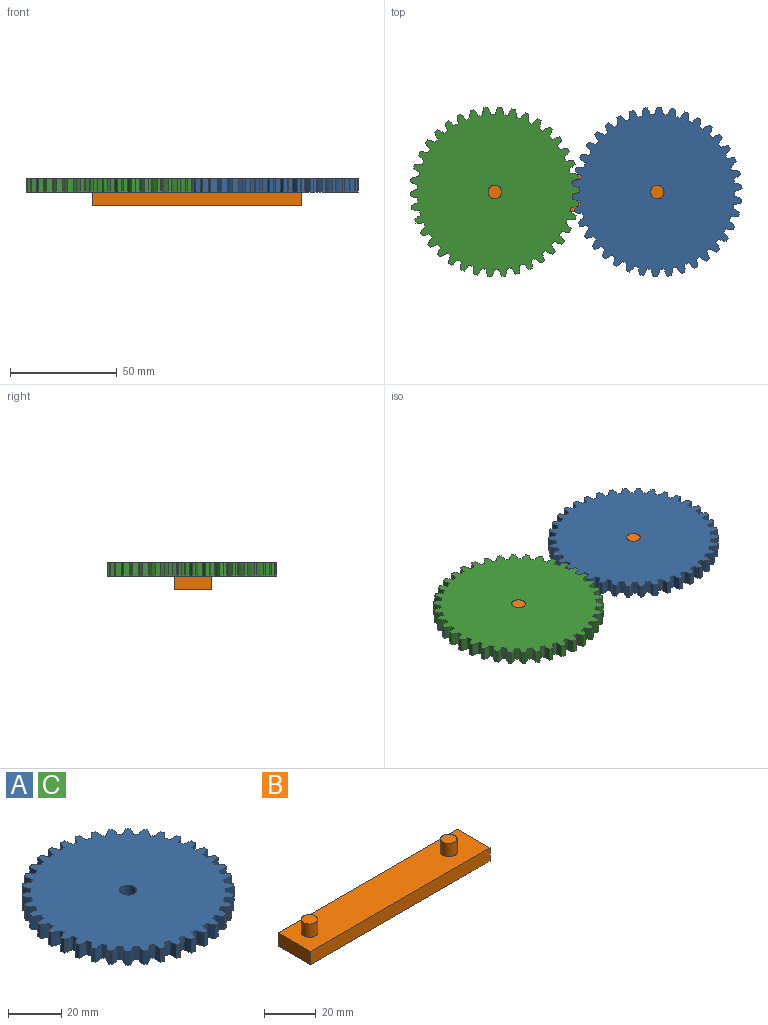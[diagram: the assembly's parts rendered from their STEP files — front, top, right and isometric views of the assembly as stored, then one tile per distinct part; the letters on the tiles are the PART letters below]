
ASSEMBLY  parts=3 mates=2
PART A: 231 faces, bbox 79.6x79.6x6.3 mm
  f0: cylinder r=36.44mm len=6.25mm, axis (0,0,-1), area 13.5mm2, adj f43,f44,f184,f189
  f1: cylinder r=36.44mm len=6.25mm, axis (0,0,-1), area 13.5mm2, adj f43,f44,f164,f169
  f2: cylinder r=36.44mm len=6.25mm, axis (0,0,-1), area 13.5mm2, adj f43,f44,f188,f194
  f3: cylinder r=36.44mm len=6.25mm, axis (0,0,-1), area 13.5mm2, adj f43,f44,f144,f149
  f4: cylinder r=36.44mm len=6.25mm, axis (0,0,-1), area 13.5mm2, adj f43,f44,f148,f154
  f5: cylinder r=36.44mm len=6.25mm, axis (0,0,-1), area 13.5mm2, adj f43,f44,f134,f139
  f6: cylinder r=36.44mm len=6.25mm, axis (0,0,-1), area 13.5mm2, adj f43,f44,f89,f94
  f7: cylinder r=36.44mm len=6.25mm, axis (0,0,-1), area 13.5mm2, adj f43,f44,f99,f104
  f8: cylinder r=36.44mm len=6.25mm, axis (0,0,-1), area 13.5mm2, adj f41,f43,f44,f59
  f9: cylinder r=36.44mm len=6.25mm, axis (0,0,-1), area 13.5mm2, adj f43,f44,f49,f54
  f10: cylinder r=36.44mm len=6.25mm, axis (0,0,-1), area 13.5mm2, adj f43,f44,f69,f74
  f11: cylinder r=36.44mm len=6.25mm, axis (0,0,-1), area 13.5mm2, adj f43,f44,f199,f204
  f12: cylinder r=36.44mm len=6.25mm, axis (0,0,-1), area 13.5mm2, adj f43,f44,f193,f198
  f13: cylinder r=36.44mm len=6.25mm, axis (0,0,-1), area 13.5mm2, adj f43,f44,f119,f124
  f14: cylinder r=36.44mm len=6.25mm, axis (0,0,-1), area 13.5mm2, adj f43,f44,f48,f225
  f15: cylinder r=36.44mm len=6.25mm, axis (0,0,-1), area 13.5mm2, adj f43,f44,f153,f159
  f16: cylinder r=36.44mm len=6.25mm, axis (0,0,-1), area 13.5mm2, adj f43,f44,f168,f174
  f17: cylinder r=36.44mm len=6.25mm, axis (0,0,-1), area 13.5mm2, adj f43,f44,f114,f118
  f18: cylinder r=36.44mm len=6.25mm, axis (0,0,-1), area 13.5mm2, adj f43,f44,f179,f183
  f19: cylinder r=36.44mm len=6.25mm, axis (0,0,-1), area 13.5mm2, adj f43,f44,f219,f224
  f20: cylinder r=36.44mm len=6.25mm, axis (0,0,-1), area 13.5mm2, adj f43,f44,f209,f214
  f21: cylinder r=36.44mm len=6.25mm, axis (0,0,-1), area 13.5mm2, adj f43,f44,f138,f143
  f22: cylinder r=36.44mm len=6.25mm, axis (0,0,-1), area 13.5mm2, adj f43,f44,f158,f163
  f23: cylinder r=36.44mm len=6.25mm, axis (0,0,-1), area 13.5mm2, adj f43,f44,f109,f113
  f24: cylinder r=36.44mm len=6.25mm, axis (0,0,-1), area 13.5mm2, adj f43,f44,f84,f88
  f25: cylinder r=36.44mm len=6.25mm, axis (0,0,-1), area 13.5mm2, adj f43,f44,f53,f58
  f26: cylinder r=36.44mm len=6.25mm, axis (0,0,-1), area 13.5mm2, adj f43,f44,f63,f68
  f27: cylinder r=36.44mm len=6.25mm, axis (0,0,-1), area 13.5mm2, adj f43,f44,f123,f129
  f28: cylinder r=36.44mm len=6.25mm, axis (0,0,-1), area 13.5mm2, adj f43,f44,f203,f208
  f29: cylinder r=36.44mm len=6.25mm, axis (0,0,-1), area 13.5mm2, adj f43,f44,f103,f108
  f30: cylinder r=36.44mm len=6.25mm, axis (0,0,-1), area 13.5mm2, adj f43,f44,f213,f218
  f31: cylinder r=36.44mm len=6.25mm, axis (0,0,-1), area 13.5mm2, adj f43,f44,f73,f79
  f32: cylinder r=36.44mm len=6.25mm, axis (0,0,-1), area 13.5mm2, adj f43,f44,f173,f178
  f33: cylinder r=36.44mm len=6.25mm, axis (0,0,-1), area 13.5mm2, adj f43,f44,f128,f133
  f34: cylinder r=36.44mm len=6.25mm, axis (0,0,-1), area 13.5mm2, adj f43,f44,f223,f229
  f35: cylinder r=36.44mm len=6.25mm, axis (0,0,-1), area 13.5mm2, adj f43,f44,f78,f83
  f36: cylinder r=36.44mm len=6.25mm, axis (0,0,-1), area 13.5mm2, adj f43,f44,f93,f98
  f37: plane 6.25x0.22mm, normal (-0.49,-0.87,0), area 1.6mm2, adj f38,f42,f43,f44
  f38: extruded ~6.25x3.21mm, area 20.6mm2, adj f37,f39,f43,f44
  f39: cylinder r=39.78mm len=6.25mm, axis (0,0,-1), area 11.2mm2, adj f38,f40,f43,f44
  f40: extruded ~6.25x2.48mm, area 20.6mm2, adj f39,f41,f43,f44
  f41: plane 6.25x0.21mm, normal (0.53,0.85,0), area 1.6mm2, adj f8,f40,f43,f44
  f42: cylinder r=36.44mm len=6.25mm, axis (0,0,-1), area 13.5mm2, adj f37,f43,f44,f64
  f43: plane 79.56x79.56mm, normal (0,0,1), area 4524.7mm2, adj f0,f1,f2,f3,f4,f5,f6,f7
  f44: plane 79.56x79.56mm, normal (0,0,-1), area 4524.7mm2, adj f0,f1,f2,f3,f4,f5,f6,f7
  f45: extruded ~6.25x3.17mm, area 20.6mm2, adj f43,f44,f46,f49
  f46: cylinder r=39.78mm len=6.25mm, axis (0,0,-1), area 11.2mm2, adj f43,f44,f45,f47
  f47: extruded ~6.25x3.08mm, area 20.6mm2, adj f43,f44,f46,f48
  f48: plane 6.25x0.25mm, normal (0.06,1,0), area 1.6mm2, adj f14,f43,f44,f47
  f49: plane 6.25x0.25mm, normal (-0.02,-1,0), area 1.6mm2, adj f9,f43,f44,f45
  f50: extruded ~6.25x3.27mm, area 20.6mm2, adj f43,f44,f51,f53
  f51: cylinder r=39.78mm len=6.25mm, axis (0,0,-1), area 11.2mm2, adj f43,f44,f50,f52
  f52: extruded ~6.25x2.85mm, area 20.6mm2, adj f43,f44,f51,f54
  f53: plane 6.25x0.25mm, normal (-0.18,-0.98,0), area 1.6mm2, adj f25,f43,f44,f50
  f54: plane 6.25x0.24mm, normal (0.23,0.97,0), area 1.6mm2, adj f9,f43,f44,f52
  f55: extruded ~6.25x3.29mm, area 20.6mm2, adj f43,f44,f56,f59
  f56: cylinder r=39.78mm len=6.25mm, axis (0,0,-1), area 11.2mm2, adj f43,f44,f55,f57
  f57: extruded ~6.25x2.54mm, area 20.6mm2, adj f43,f44,f56,f58
  f58: plane 6.25x0.23mm, normal (0.38,0.92,0), area 1.6mm2, adj f25,f43,f44,f57
  f59: plane 6.25x0.23mm, normal (-0.34,-0.94,0), area 1.6mm2, adj f8,f43,f44,f55
  f60: extruded ~6.25x3.05mm, area 20.6mm2, adj f43,f44,f61,f63
  f61: cylinder r=39.78mm len=6.25mm, axis (0,0,-1), area 11.2mm2, adj f43,f44,f60,f62
  f62: extruded ~6.25x2.8mm, area 20.6mm2, adj f43,f44,f61,f64
  f63: plane 6.25x0.19mm, normal (-0.63,-0.78,0), area 1.6mm2, adj f26,f43,f44,f60
  f64: plane 6.25x0.19mm, normal (0.66,0.75,0), area 1.6mm2, adj f42,f43,f44,f62
  f65: extruded ~6.25x2.8mm, area 20.6mm2, adj f43,f44,f66,f69
  f66: cylinder r=39.78mm len=6.25mm, axis (0,0,-1), area 11.2mm2, adj f43,f44,f65,f67
  f67: extruded ~6.25x3.05mm, area 20.6mm2, adj f43,f44,f66,f68
  f68: plane 6.25x0.19mm, normal (0.78,0.63,0), area 1.6mm2, adj f26,f43,f44,f67
  f69: plane 6.25x0.19mm, normal (-0.75,-0.66,0), area 1.6mm2, adj f10,f43,f44,f65
  f70: extruded ~6.25x2.48mm, area 20.6mm2, adj f43,f44,f71,f73
  f71: cylinder r=39.78mm len=6.25mm, axis (0,0,-1), area 11.2mm2, adj f43,f44,f70,f72
  f72: extruded ~6.25x3.21mm, area 20.6mm2, adj f43,f44,f71,f74
  f73: plane 6.25x0.21mm, normal (-0.85,-0.53,0), area 1.6mm2, adj f31,f43,f44,f70
  f74: plane 6.25x0.22mm, normal (0.87,0.49,0), area 1.6mm2, adj f10,f43,f44,f72
  f75: extruded ~6.25x2.54mm, area 20.6mm2, adj f43,f44,f76,f78
  f76: cylinder r=39.78mm len=6.25mm, axis (0,0,-1), area 11.2mm2, adj f43,f44,f75,f77
  f77: extruded ~6.25x3.29mm, area 20.6mm2, adj f43,f44,f76,f79
  f78: plane 6.25x0.23mm, normal (-0.92,-0.38,0), area 1.6mm2, adj f35,f43,f44,f75
  f79: plane 6.25x0.23mm, normal (0.94,0.34,0), area 1.6mm2, adj f31,f43,f44,f77
  f80: extruded ~6.25x2.85mm, area 20.6mm2, adj f43,f44,f81,f84
  f81: cylinder r=39.78mm len=6.25mm, axis (0,0,-1), area 11.2mm2, adj f43,f44,f80,f82
  f82: extruded ~6.25x3.27mm, area 20.6mm2, adj f43,f44,f81,f83
  f83: plane 6.25x0.25mm, normal (0.98,0.18,0), area 1.6mm2, adj f35,f43,f44,f82
  f84: plane 6.25x0.24mm, normal (-0.97,-0.23,0), area 1.6mm2, adj f24,f43,f44,f80
  f85: extruded ~6.25x3.08mm, area 20.6mm2, adj f43,f44,f86,f89
  f86: cylinder r=39.78mm len=6.25mm, axis (0,0,-1), area 11.2mm2, adj f43,f44,f85,f87
  f87: extruded ~6.25x3.17mm, area 20.6mm2, adj f43,f44,f86,f88
  f88: plane 6.25x0.25mm, normal (1,0.02,0), area 1.6mm2, adj f24,f43,f44,f87
  f89: plane 6.25x0.25mm, normal (-1,-0.06,0), area 1.6mm2, adj f6,f43,f44,f85
  f90: extruded ~6.25x3.23mm, area 20.6mm2, adj f43,f44,f91,f93
  f91: cylinder r=39.78mm len=6.25mm, axis (0,0,-1), area 11.2mm2, adj f43,f44,f90,f92
  f92: extruded ~6.25x2.98mm, area 20.6mm2, adj f43,f44,f91,f94
  f93: plane 6.25x0.25mm, normal (-0.99,0.1,0), area 1.6mm2, adj f36,f43,f44,f90
  f94: plane 6.25x0.25mm, normal (0.99,-0.14,0), area 1.6mm2, adj f6,f43,f44,f92
  f95: extruded ~6.25x3.29mm, area 20.6mm2, adj f43,f44,f96,f99
  f96: cylinder r=39.78mm len=6.25mm, axis (0,0,-1), area 11.2mm2, adj f43,f44,f95,f97
  f97: extruded ~6.25x2.7mm, area 20.6mm2, adj f43,f44,f96,f98
  f98: plane 6.25x0.24mm, normal (0.95,-0.31,0), area 1.6mm2, adj f36,f43,f44,f97
  f99: plane 6.25x0.24mm, normal (-0.96,0.27,0), area 1.6mm2, adj f7,f43,f44,f95
  f100: extruded ~6.25x3.26mm, area 20.6mm2, adj f43,f44,f101,f103
  f101: cylinder r=39.78mm len=6.25mm, axis (0,0,-1), area 11.2mm2, adj f43,f44,f100,f102
  f102: extruded ~6.25x2.36mm, area 20.6mm2, adj f43,f44,f101,f104
  f103: plane 6.25x0.23mm, normal (-0.91,0.42,0), area 1.6mm2, adj f29,f43,f44,f100
  f104: plane 6.25x0.22mm, normal (0.89,-0.46,0), area 1.6mm2, adj f7,f43,f44,f102
  f105: extruded ~6.25x3.14mm, area 20.6mm2, adj f43,f44,f106,f109
  f106: cylinder r=39.78mm len=6.25mm, axis (0,0,-1), area 11.2mm2, adj f43,f44,f105,f107
  f107: extruded ~6.25x2.65mm, area 20.6mm2, adj f43,f44,f106,f108
  f108: plane 6.25x0.2mm, normal (0.8,-0.6,0), area 1.6mm2, adj f29,f43,f44,f107
  f109: plane 6.25x0.21mm, normal (-0.83,0.56,0), area 1.6mm2, adj f23,f43,f44,f105
  f110: extruded ~6.25x2.94mm, area 20.6mm2, adj f43,f44,f111,f114
  f111: cylinder r=39.78mm len=6.25mm, axis (0,0,-1), area 11.2mm2, adj f43,f44,f110,f112
  f112: extruded ~6.25x2.94mm, area 20.6mm2, adj f43,f44,f111,f113
  f113: plane 6.25x0.18mm, normal (0.69,-0.72,0), area 1.6mm2, adj f23,f43,f44,f112
  f114: plane 6.25x0.18mm, normal (-0.72,0.69,0), area 1.6mm2, adj f17,f43,f44,f110
  f115: extruded ~6.25x2.65mm, area 20.6mm2, adj f43,f44,f116,f119
  f116: cylinder r=39.78mm len=6.25mm, axis (0,0,-1), area 11.2mm2, adj f43,f44,f115,f117
  f117: extruded ~6.25x3.14mm, area 20.6mm2, adj f43,f44,f116,f118
  f118: plane 6.25x0.21mm, normal (0.56,-0.83,0), area 1.6mm2, adj f17,f43,f44,f117
  f119: plane 6.25x0.2mm, normal (-0.6,0.8,0), area 1.6mm2, adj f13,f43,f44,f115
  f120: extruded ~6.25x2.36mm, area 20.6mm2, adj f43,f44,f121,f123
  f121: cylinder r=39.78mm len=6.25mm, axis (0,0,-1), area 11.2mm2, adj f43,f44,f120,f122
  f122: extruded ~6.25x3.26mm, area 20.6mm2, adj f43,f44,f121,f124
  f123: plane 6.25x0.22mm, normal (-0.46,0.89,0), area 1.6mm2, adj f27,f43,f44,f120
  f124: plane 6.25x0.23mm, normal (0.42,-0.91,0), area 1.6mm2, adj f13,f43,f44,f122
  f125: extruded ~6.25x2.7mm, area 20.6mm2, adj f43,f44,f126,f128
  f126: cylinder r=39.78mm len=6.25mm, axis (0,0,-1), area 11.2mm2, adj f43,f44,f125,f127
  f127: extruded ~6.25x3.29mm, area 20.6mm2, adj f43,f44,f126,f129
  f128: plane 6.25x0.24mm, normal (-0.31,0.95,0), area 1.6mm2, adj f33,f43,f44,f125
  f129: plane 6.25x0.24mm, normal (0.27,-0.96,0), area 1.6mm2, adj f27,f43,f44,f127
  f130: extruded ~6.25x2.98mm, area 20.6mm2, adj f43,f44,f131,f134
  f131: cylinder r=39.78mm len=6.25mm, axis (0,0,-1), area 11.2mm2, adj f43,f44,f130,f132
  f132: extruded ~6.25x3.23mm, area 20.6mm2, adj f43,f44,f131,f133
  f133: plane 6.25x0.25mm, normal (0.1,-0.99,0), area 1.6mm2, adj f33,f43,f44,f132
  f134: plane 6.25x0.25mm, normal (-0.14,0.99,0), area 1.6mm2, adj f5,f43,f44,f130
  f135: extruded ~6.25x3.17mm, area 20.6mm2, adj f43,f44,f136,f138
  f136: cylinder r=39.78mm len=6.25mm, axis (0,0,-1), area 11.2mm2, adj f43,f44,f135,f137
  f137: extruded ~6.25x3.08mm, area 20.6mm2, adj f43,f44,f136,f139
  f138: plane 6.25x0.25mm, normal (0.02,1,0), area 1.6mm2, adj f21,f43,f44,f135
  f139: plane 6.25x0.25mm, normal (-0.06,-1,0), area 1.6mm2, adj f5,f43,f44,f137
  f140: extruded ~6.25x3.27mm, area 20.6mm2, adj f43,f44,f141,f144
  f141: cylinder r=39.78mm len=6.25mm, axis (0,0,-1), area 11.2mm2, adj f43,f44,f140,f142
  f142: extruded ~6.25x2.85mm, area 20.6mm2, adj f43,f44,f141,f143
  f143: plane 6.25x0.24mm, normal (-0.23,-0.97,0), area 1.6mm2, adj f21,f43,f44,f142
  f144: plane 6.25x0.25mm, normal (0.18,0.98,0), area 1.6mm2, adj f3,f43,f44,f140
  f145: extruded ~6.25x3.29mm, area 20.6mm2, adj f43,f44,f146,f148
  f146: cylinder r=39.78mm len=6.25mm, axis (0,0,-1), area 11.2mm2, adj f43,f44,f145,f147
  f147: extruded ~6.25x2.54mm, area 20.6mm2, adj f43,f44,f146,f149
  f148: plane 6.25x0.23mm, normal (0.34,0.94,0), area 1.6mm2, adj f4,f43,f44,f145
  f149: plane 6.25x0.23mm, normal (-0.38,-0.92,0), area 1.6mm2, adj f3,f43,f44,f147
  f150: extruded ~6.25x3.21mm, area 20.6mm2, adj f43,f44,f151,f153
  f151: cylinder r=39.78mm len=6.25mm, axis (0,0,-1), area 11.2mm2, adj f43,f44,f150,f152
  f152: extruded ~6.25x2.48mm, area 20.6mm2, adj f43,f44,f151,f154
  f153: plane 6.25x0.22mm, normal (0.49,0.87,0), area 1.6mm2, adj f15,f43,f44,f150
  f154: plane 6.25x0.21mm, normal (-0.53,-0.85,0), area 1.6mm2, adj f4,f43,f44,f152
  f155: extruded ~6.25x3.05mm, area 20.6mm2, adj f43,f44,f156,f158
  f156: cylinder r=39.78mm len=6.25mm, axis (0,0,-1), area 11.2mm2, adj f43,f44,f155,f157
  f157: extruded ~6.25x2.8mm, area 20.6mm2, adj f43,f44,f156,f159
  f158: plane 6.25x0.19mm, normal (0.63,0.78,0), area 1.6mm2, adj f22,f43,f44,f155
  f159: plane 6.25x0.19mm, normal (-0.66,-0.75,0), area 1.6mm2, adj f15,f43,f44,f157
  f160: extruded ~6.25x2.8mm, area 20.6mm2, adj f43,f44,f161,f164
  f161: cylinder r=39.78mm len=6.25mm, axis (0,0,-1), area 11.2mm2, adj f43,f44,f160,f162
  f162: extruded ~6.25x3.05mm, area 20.6mm2, adj f43,f44,f161,f163
  f163: plane 6.25x0.19mm, normal (-0.78,-0.63,0), area 1.6mm2, adj f22,f43,f44,f162
  f164: plane 6.25x0.19mm, normal (0.75,0.66,0), area 1.6mm2, adj f1,f43,f44,f160
  f165: extruded ~6.25x2.48mm, area 20.6mm2, adj f43,f44,f166,f168
  f166: cylinder r=39.78mm len=6.25mm, axis (0,0,-1), area 11.2mm2, adj f43,f44,f165,f167
  f167: extruded ~6.25x3.21mm, area 20.6mm2, adj f43,f44,f166,f169
  f168: plane 6.25x0.21mm, normal (0.85,0.53,0), area 1.6mm2, adj f16,f43,f44,f165
  f169: plane 6.25x0.22mm, normal (-0.87,-0.49,0), area 1.6mm2, adj f1,f43,f44,f167
  f170: extruded ~6.25x2.54mm, area 20.6mm2, adj f43,f44,f171,f173
  f171: cylinder r=39.78mm len=6.25mm, axis (0,0,-1), area 11.2mm2, adj f43,f44,f170,f172
  f172: extruded ~6.25x3.29mm, area 20.6mm2, adj f43,f44,f171,f174
  f173: plane 6.25x0.23mm, normal (0.92,0.38,0), area 1.6mm2, adj f32,f43,f44,f170
  f174: plane 6.25x0.23mm, normal (-0.94,-0.34,0), area 1.6mm2, adj f16,f43,f44,f172
  f175: extruded ~6.25x2.85mm, area 20.6mm2, adj f43,f44,f176,f179
  f176: cylinder r=39.78mm len=6.25mm, axis (0,0,-1), area 11.2mm2, adj f43,f44,f175,f177
  f177: extruded ~6.25x3.27mm, area 20.6mm2, adj f43,f44,f176,f178
  f178: plane 6.25x0.25mm, normal (-0.98,-0.18,0), area 1.6mm2, adj f32,f43,f44,f177
  f179: plane 6.25x0.24mm, normal (0.97,0.23,0), area 1.6mm2, adj f18,f43,f44,f175
  f180: extruded ~6.25x3.08mm, area 20.6mm2, adj f43,f44,f181,f184
  f181: cylinder r=39.78mm len=6.25mm, axis (0,0,-1), area 11.2mm2, adj f43,f44,f180,f182
  f182: extruded ~6.25x3.17mm, area 20.6mm2, adj f43,f44,f181,f183
  f183: plane 6.25x0.25mm, normal (-1,-0.02,0), area 1.6mm2, adj f18,f43,f44,f182
  f184: plane 6.25x0.25mm, normal (1,0.06,0), area 1.6mm2, adj f0,f43,f44,f180
  f185: extruded ~6.25x3.23mm, area 20.6mm2, adj f43,f44,f186,f188
  f186: cylinder r=39.78mm len=6.25mm, axis (0,0,-1), area 11.2mm2, adj f43,f44,f185,f187
  f187: extruded ~6.25x2.98mm, area 20.6mm2, adj f43,f44,f186,f189
  f188: plane 6.25x0.25mm, normal (0.99,-0.1,0), area 1.6mm2, adj f2,f43,f44,f185
  f189: plane 6.25x0.25mm, normal (-0.99,0.14,0), area 1.6mm2, adj f0,f43,f44,f187
  f190: extruded ~6.25x3.29mm, area 20.6mm2, adj f43,f44,f191,f193
  f191: cylinder r=39.78mm len=6.25mm, axis (0,0,-1), area 11.2mm2, adj f43,f44,f190,f192
  f192: extruded ~6.25x2.7mm, area 20.6mm2, adj f43,f44,f191,f194
  f193: plane 6.25x0.24mm, normal (0.96,-0.27,0), area 1.6mm2, adj f12,f43,f44,f190
  f194: plane 6.25x0.24mm, normal (-0.95,0.31,0), area 1.6mm2, adj f2,f43,f44,f192
  f195: extruded ~6.25x3.26mm, area 20.6mm2, adj f43,f44,f196,f199
  f196: cylinder r=39.78mm len=6.25mm, axis (0,0,-1), area 11.2mm2, adj f43,f44,f195,f197
  f197: extruded ~6.25x2.36mm, area 20.6mm2, adj f43,f44,f196,f198
  f198: plane 6.25x0.22mm, normal (-0.89,0.46,0), area 1.6mm2, adj f12,f43,f44,f197
  f199: plane 6.25x0.23mm, normal (0.91,-0.42,0), area 1.6mm2, adj f11,f43,f44,f195
  f200: extruded ~6.25x3.14mm, area 20.6mm2, adj f43,f44,f201,f203
  f201: cylinder r=39.78mm len=6.25mm, axis (0,0,-1), area 11.2mm2, adj f43,f44,f200,f202
  f202: extruded ~6.25x2.65mm, area 20.6mm2, adj f43,f44,f201,f204
  f203: plane 6.25x0.21mm, normal (0.83,-0.56,0), area 1.6mm2, adj f28,f43,f44,f200
  f204: plane 6.25x0.2mm, normal (-0.8,0.6,0), area 1.6mm2, adj f11,f43,f44,f202
  f205: extruded ~6.25x2.94mm, area 20.6mm2, adj f43,f44,f206,f209
  f206: cylinder r=39.78mm len=6.25mm, axis (0,0,-1), area 11.2mm2, adj f43,f44,f205,f207
  f207: extruded ~6.25x2.94mm, area 20.6mm2, adj f43,f44,f206,f208
  f208: plane 6.25x0.18mm, normal (-0.69,0.72,0), area 1.6mm2, adj f28,f43,f44,f207
  f209: plane 6.25x0.18mm, normal (0.72,-0.69,0), area 1.6mm2, adj f20,f43,f44,f205
  f210: extruded ~6.25x2.65mm, area 20.6mm2, adj f43,f44,f211,f213
  f211: cylinder r=39.78mm len=6.25mm, axis (0,0,-1), area 11.2mm2, adj f43,f44,f210,f212
  f212: extruded ~6.25x3.14mm, area 20.6mm2, adj f43,f44,f211,f214
  f213: plane 6.25x0.2mm, normal (0.6,-0.8,0), area 1.6mm2, adj f30,f43,f44,f210
  f214: plane 6.25x0.21mm, normal (-0.56,0.83,0), area 1.6mm2, adj f20,f43,f44,f212
  f215: extruded ~6.25x2.36mm, area 20.6mm2, adj f43,f44,f216,f219
  f216: cylinder r=39.78mm len=6.25mm, axis (0,0,-1), area 11.2mm2, adj f43,f44,f215,f217
  f217: extruded ~6.25x3.26mm, area 20.6mm2, adj f43,f44,f216,f218
  f218: plane 6.25x0.23mm, normal (-0.42,0.91,0), area 1.6mm2, adj f30,f43,f44,f217
  f219: plane 6.25x0.22mm, normal (0.46,-0.89,0), area 1.6mm2, adj f19,f43,f44,f215
  f220: extruded ~6.25x2.7mm, area 20.6mm2, adj f43,f44,f221,f223
  f221: cylinder r=39.78mm len=6.25mm, axis (0,0,-1), area 11.2mm2, adj f43,f44,f220,f222
  f222: extruded ~6.25x3.29mm, area 20.6mm2, adj f43,f44,f221,f224
  f223: plane 6.25x0.24mm, normal (0.31,-0.95,0), area 1.6mm2, adj f34,f43,f44,f220
  f224: plane 6.25x0.24mm, normal (-0.27,0.96,0), area 1.6mm2, adj f19,f43,f44,f222
  f225: plane 6.25x0.25mm, normal (0.14,-0.99,0), area 1.6mm2, adj f14,f43,f44,f226
  f226: extruded ~6.25x2.98mm, area 20.6mm2, adj f43,f44,f225,f227
  f227: cylinder r=39.78mm len=6.25mm, axis (0,0,-1), area 11.2mm2, adj f43,f44,f226,f228
  f228: extruded ~6.25x3.23mm, area 20.6mm2, adj f43,f44,f227,f229
  f229: plane 6.25x0.25mm, normal (-0.1,0.99,0), area 1.6mm2, adj f34,f43,f44,f228
  f230: cylinder r=3.17mm len=6.35mm, axis (0,0,-1), area 124.7mm2, adj f43,f44
PART B: 10 faces, bbox 98.2x17.7x12.5 mm
  f0: plane 17.71x6.25mm, normal (-1,0,0), area 110.7mm2, adj f1,f3,f4,f5
  f1: plane 98.17x6.25mm, normal (0,-1,0), area 613.6mm2, adj f0,f2,f4,f5
  f2: plane 17.71x6.25mm, normal (1,0,0), area 110.7mm2, adj f1,f3,f4,f5
  f3: plane 98.17x6.25mm, normal (0,1,0), area 613.6mm2, adj f0,f2,f4,f5
  f4: plane 98.17x17.71mm, normal (0,0,-1), area 1738.2mm2, adj f0,f1,f2,f3
  f5: plane 98.17x17.71mm, normal (0,0,1), area 1674.9mm2, adj f0,f1,f2,f3,f6,f8
  f6: cylinder r=3.17mm len=6.35mm, axis (0,0,-1), area 124.7mm2, adj f5,f7
  f7: plane 6.35x6.35mm, normal (0,0,1), area 31.7mm2, adj f6
  f8: cylinder r=3.17mm len=6.35mm, axis (0,0,-1), area 124.7mm2, adj f5,f9
  f9: plane 6.35x6.35mm, normal (0,0,1), area 31.7mm2, adj f8
PART C: same geometry as A
PLACE A rot(axis=(0,0,1),119.5deg) t=(0,0,0)mm
PLACE B at identity fixed
PLACE C rot(axis=(0.97,-0.25,0),180deg) t=(-76.2,0,6.25)mm
MATE revolute C.f230 <-> B.f8  axis (0,0,-1) through (-76.2,0,0)mm
MATE revolute A.f61 <-> B.f6  axis (0,0,1) through (0,0,6.25)mm
